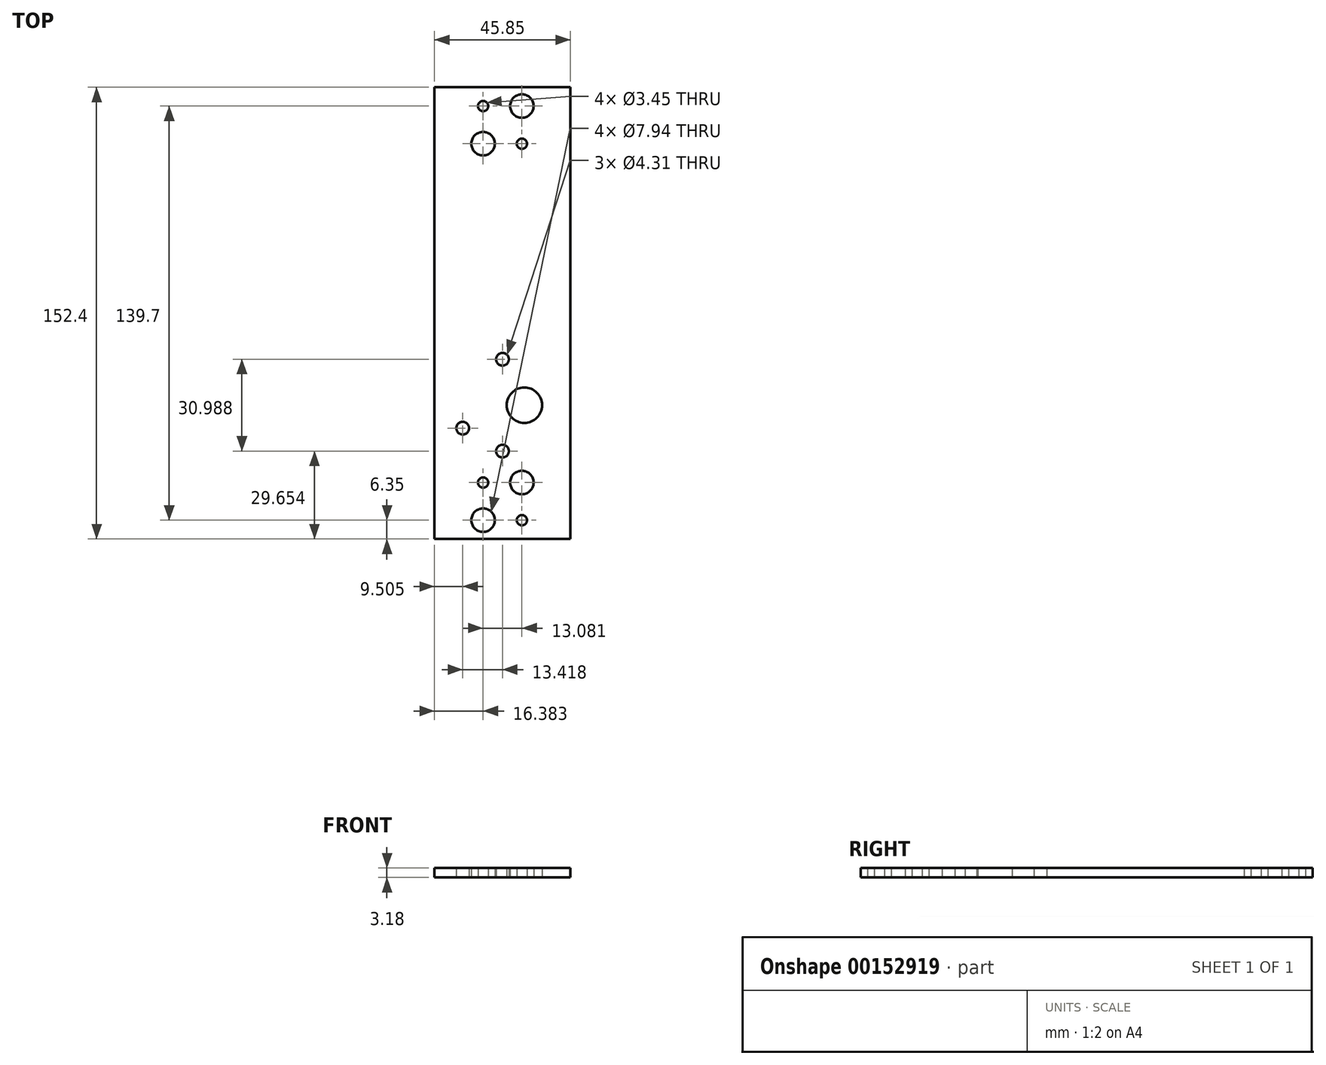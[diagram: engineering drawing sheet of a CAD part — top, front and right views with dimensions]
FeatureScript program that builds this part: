
annotation { "Feature Type Name" : "Feature", "Feature Type Description" : "" }
export const myFeature = defineFeature(function(context is Context, id is Id, definition is map)
    precondition{}
    {
        {
            var Q0;
            Q0=qCreatedBy(makeId("Top.planeOp"),FACE);
            var sketch = newSketch(context, id + "F0", { "sketchPlane" : qUnion([Q0])});
            skLineSegment(sketch, "E0.bottom", {"start": v(0, 0) * mm, "end": v(45.85, 0) * mm});
            skLineSegment(sketch, "E0.top", {"start": v(0, -152.4) * mm, "end": v(45.85, -152.4) * mm});
            skLineSegment(sketch, "E0.left", {"start": v(0, 0) * mm, "end": v(0, -152.4) * mm});
            skLineSegment(sketch, "E0.right", {"start": v(45.85, 0) * mm, "end": v(45.85, -152.4) * mm});
            skLineSegment(sketch, "E1", {"start": v(16.38, 0) * mm, "end": v(16.38, -6.35) * mm, "construction": true});
            skLineSegment(sketch, "E2", {"start": v(16.38, -6.35) * mm, "end": v(0, -6.35) * mm, "construction": true});
            skCircle(sketch, "E3", {"center": v(16.38, -6.35) * mm, "radius": 1.73 * mm});
            skLineSegment(sketch, "E4", {"start": v(16.38, -6.35) * mm, "end": v(16.38, -19.05) * mm, "construction": true});
            skCircle(sketch, "E5", {"center": v(16.38, -19.05) * mm, "radius": 3.97 * mm});
            skLineSegment(sketch, "E6", {"start": v(16.38, -152.4) * mm, "end": v(16.38, -146.05) * mm, "construction": true});
            skLineSegment(sketch, "E7", {"start": v(16.38, -146.05) * mm, "end": v(16.38, -133.35) * mm, "construction": true});
            skCircle(sketch, "E8", {"center": v(16.38, -133.35) * mm, "radius": 1.73 * mm});
            skCircle(sketch, "E9", {"center": v(16.38, -146.05) * mm, "radius": 3.97 * mm});
            skLineSegment(sketch, "E10", {"start": v(45.85, -6.35) * mm, "end": v(29.46, -6.35) * mm, "construction": true});
            skLineSegment(sketch, "E11", {"start": v(29.46, -6.35) * mm, "end": v(29.46, 0) * mm, "construction": true});
            skLineSegment(sketch, "E12", {"start": v(29.46, -6.35) * mm, "end": v(29.46, -19.05) * mm, "construction": true});
            skLineSegment(sketch, "E13", {"start": v(29.46, -152.4) * mm, "end": v(29.46, -146.05) * mm, "construction": true});
            skLineSegment(sketch, "E14", {"start": v(29.46, -146.05) * mm, "end": v(29.46, -133.35) * mm, "construction": true});
            skCircle(sketch, "E15", {"center": v(29.46, -6.35) * mm, "radius": 3.97 * mm});
            skCircle(sketch, "E16", {"center": v(29.46, -19.05) * mm, "radius": 1.73 * mm});
            skCircle(sketch, "E17", {"center": v(29.46, -133.35) * mm, "radius": 3.97 * mm});
            skCircle(sketch, "E18", {"center": v(29.46, -146.05) * mm, "radius": 1.73 * mm});
            skCircle(sketch, "E19", {"center": v(22.92, -107.25) * mm, "radius": 18.16 * mm, "construction": true});
            skCircle(sketch, "E20.cCircle", {"center": v(22.92, -107.25) * mm, "radius": 13.42 * mm, "construction": true});
            skLineSegment(sketch, "E20.0", {"start": v(36.34, -99.5) * mm, "end": v(36.34, -115) * mm, "construction": true});
            skLineSegment(sketch, "E20.1", {"start": v(36.34, -115) * mm, "end": v(22.92, -122.75) * mm, "construction": true});
            skLineSegment(sketch, "E20.2", {"start": v(22.92, -122.75) * mm, "end": v(9.5, -115) * mm, "construction": true});
            skLineSegment(sketch, "E20.3", {"start": v(9.5, -115) * mm, "end": v(9.5, -99.5) * mm, "construction": true});
            skLineSegment(sketch, "E20.4", {"start": v(9.5, -99.5) * mm, "end": v(22.92, -91.76) * mm, "construction": true});
            skLineSegment(sketch, "E20.5", {"start": v(22.92, -91.76) * mm, "end": v(36.34, -99.5) * mm, "construction": true});
            skPoint(sketch, "E20.0.midPoint", {"position": v(36.34, -107.25) * mm});
            skCircle(sketch, "E21", {"center": v(9.5, -115) * mm, "radius": 2.15 * mm});
            skCircle(sketch, "E22", {"center": v(22.92, -122.75) * mm, "radius": 2.15 * mm});
            skCircle(sketch, "E23", {"center": v(22.92, -91.76) * mm, "radius": 2.15 * mm});
            skLineSegment(sketch, "E24", {"start": v(22.92, -107.25) * mm, "end": v(30.29, -107.25) * mm, "construction": true});
            skCircle(sketch, "E25", {"center": v(30.29, -107.25) * mm, "radius": 5.97 * mm});
            skLineSegment(sketch, "E26", {"start": v(30.29, -107.25) * mm, "end": v(41.08, -107.25) * mm, "construction": true});
            skLineSegment(sketch, "E27", {"start": v(41.08, -107.25) * mm, "end": v(45.85, -107.25) * mm, "construction": true});
            skLineSegment(sketch, "E28", {"start": v(29.46, -133.35) * mm, "end": v(23.11, -133.35) * mm, "construction": true});
            skLineSegment(sketch, "E29", {"start": v(23.11, -133.35) * mm, "end": v(23.11, -125.41) * mm, "construction": true});
            skLineSegment(sketch, "E30", {"start": v(22.92, -107.25) * mm, "end": v(4.76, -107.25) * mm, "construction": true});
            skLineSegment(sketch, "E31", {"start": v(4.76, -107.25) * mm, "end": v(0, -107.25) * mm, "construction": true});
            skSolve(sketch);
        }
        {
            var Q0;
            Q0=makeQuery(id+"F0.imprint","IMPRINT",FACE,{"disambiguationData":[TD([[makeQuery(id+"F0.imprint","IMPRINT",EDGE,{"derivedFrom":sQuery(id+"F0.wireOp",EDGE,"E0.bottom")}),-1.0]])]});
            extrude(context, id + "F1", {"entities" : qUnion([Q0]), "depth" : 3.17 * mm});
        }
    });
